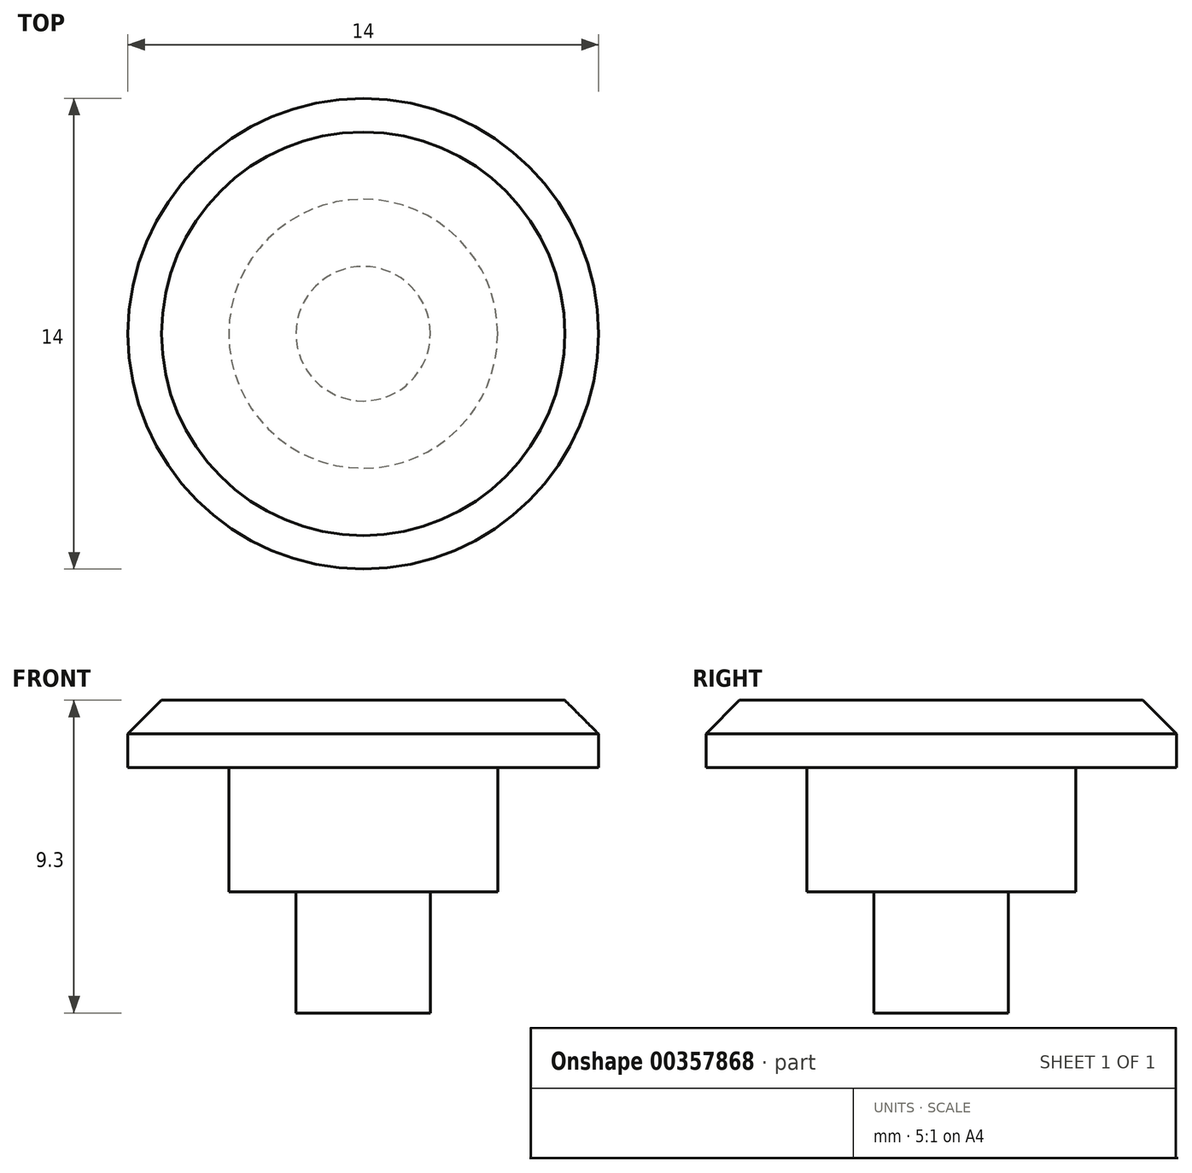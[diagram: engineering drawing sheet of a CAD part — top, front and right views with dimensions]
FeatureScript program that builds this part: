
annotation { "Feature Type Name" : "Feature", "Feature Type Description" : "" }
export const myFeature = defineFeature(function(context is Context, id is Id, definition is map)
    precondition{}
    {
        {
            var Q0;
            Q0=qCreatedBy(makeId("Top.planeOp"),FACE);
            var sketch = newSketch(context, id + "F0", { "sketchPlane" : qUnion([Q0])});
            skCircle(sketch, "E0", {"center": v(0, 0) * mm, "radius": 7 * mm});
            skCircle(sketch, "E1", {"center": v(0, 0) * mm, "radius": 4 * mm});
            skCircle(sketch, "E2", {"center": v(0, 0) * mm, "radius": 2 * mm});
            skSolve(sketch);
        }
        {
            var Q0;
            Q0 = qSketchRegion(id + "F0", true);
            var Q1;
            Q1=makeQuery(id+"F0.imprint","IMPRINT",FACE,{"disambiguationData":[TD([[makeQuery(id+"F0.imprint","IMPRINT",EDGE,{"derivedFrom":sQuery(id+"F0.wireOp",EDGE,"E1")}),1.0]])]});
            var Q2;
            Q2=makeQuery(id+"F0.imprint","IMPRINT",FACE,{"disambiguationData":[TD([[makeQuery(id+"F0.imprint","IMPRINT",EDGE,{"derivedFrom":sQuery(id+"F0.wireOp",EDGE,"E2")}),1.0]])]});
            extrude(context, id + "F1", {"entities" : qUnion([Q0, Q1, Q2]), "depth" : 2 * mm});
        }
        {
            var Q0;
            Q0=makeQuery(id+"F1.opExtrude","CAP_EDGE",EDGE,{"disambiguationData":[OSD([sQuery(id+"F0.wireOp",EDGE,"E0")])],"isStart":false});
            chamfer(context, id + "F2", {"entities" : qUnion([Q0]), "width" : 1 * mm, "tangentPropagation" : true});
        }
        {
            var Q0;
            Q0=makeQuery(id+"F0.imprint","IMPRINT",FACE,{"disambiguationData":[TD([[makeQuery(id+"F0.imprint","IMPRINT",EDGE,{"derivedFrom":sQuery(id+"F0.wireOp",EDGE,"E2")}),1.0]])]});
            extrude(context, id + "F3", {"entities" : qUnion([Q0]), "operationType" : NewBodyOperationType.ADD, "depth" : -7.3 * mm});
        }
        {
            var Q0;
            Q0=makeQuery(id+"F0.imprint","IMPRINT",FACE,{"disambiguationData":[TD([[makeQuery(id+"F0.imprint","IMPRINT",EDGE,{"derivedFrom":sQuery(id+"F0.wireOp",EDGE,"E1")}),1.0]])]});
            extrude(context, id + "F4", {"entities" : qUnion([Q0]), "operationType" : NewBodyOperationType.ADD, "depth" : -3.7 * mm});
        }
    });
